# Revit family: Fuse
name_source: partatom
category: Lighting Fixtures
revit_build: Autodesk Revit 2018 (Build: 20170927_1515(x64)
units: mm (PartAtom-declared; Revit-internal decimal feet)

## family parameters
Always vertical = Yes
Cut with Voids When Loaded = No
Host = Wall
Light Source = Yes
OmniClass Number = 23.80.70.00
OmniClass Title = Lighting
Part Type = Normal
Room Calculation Point = No
Round Connector Dimension = Use Diameter
Shared = No

## types (2) — shared parameters
Color Filter = 16777215
Dimming Lamp Color Temperature Shift = <None>
Driver Required = No
Main Material = Metal - Steel
Manufacturer = Astro Lighting Ltd
URL = www.astrolighting.com

## per-type parameters (varying)
| type | ADA compliant | Apparent Load | Dimmable | Dimming Method | Driver Included | Efficacy (lm/w) | Electrical Class | Lamp | Light Source Fixed | Location rating | Main Finish | Photometric Web File | Power (Watts) | Product Code | Product Location | Product Name | Product SKU | Tilt Angle |
| CE | No | 8 VA | No | Not Applicable | Yes | 39 | 1 | LED | Yes | IP20 | Various | GNC-2113 Fuse LED.ies | 4.4 | 8395 | Indoor | Fuse | 1215050 | 0.00° |
| ETL | NO | 0 VA |  |  |  |  | 0 |  |  | DAMP |  | generic |  | 1234 | Bathroom |  | 1234001 | 60.00° |

## geometry (parser evidence)
native form markers: Sweep x2
no freeform markers — native parametric forms only
